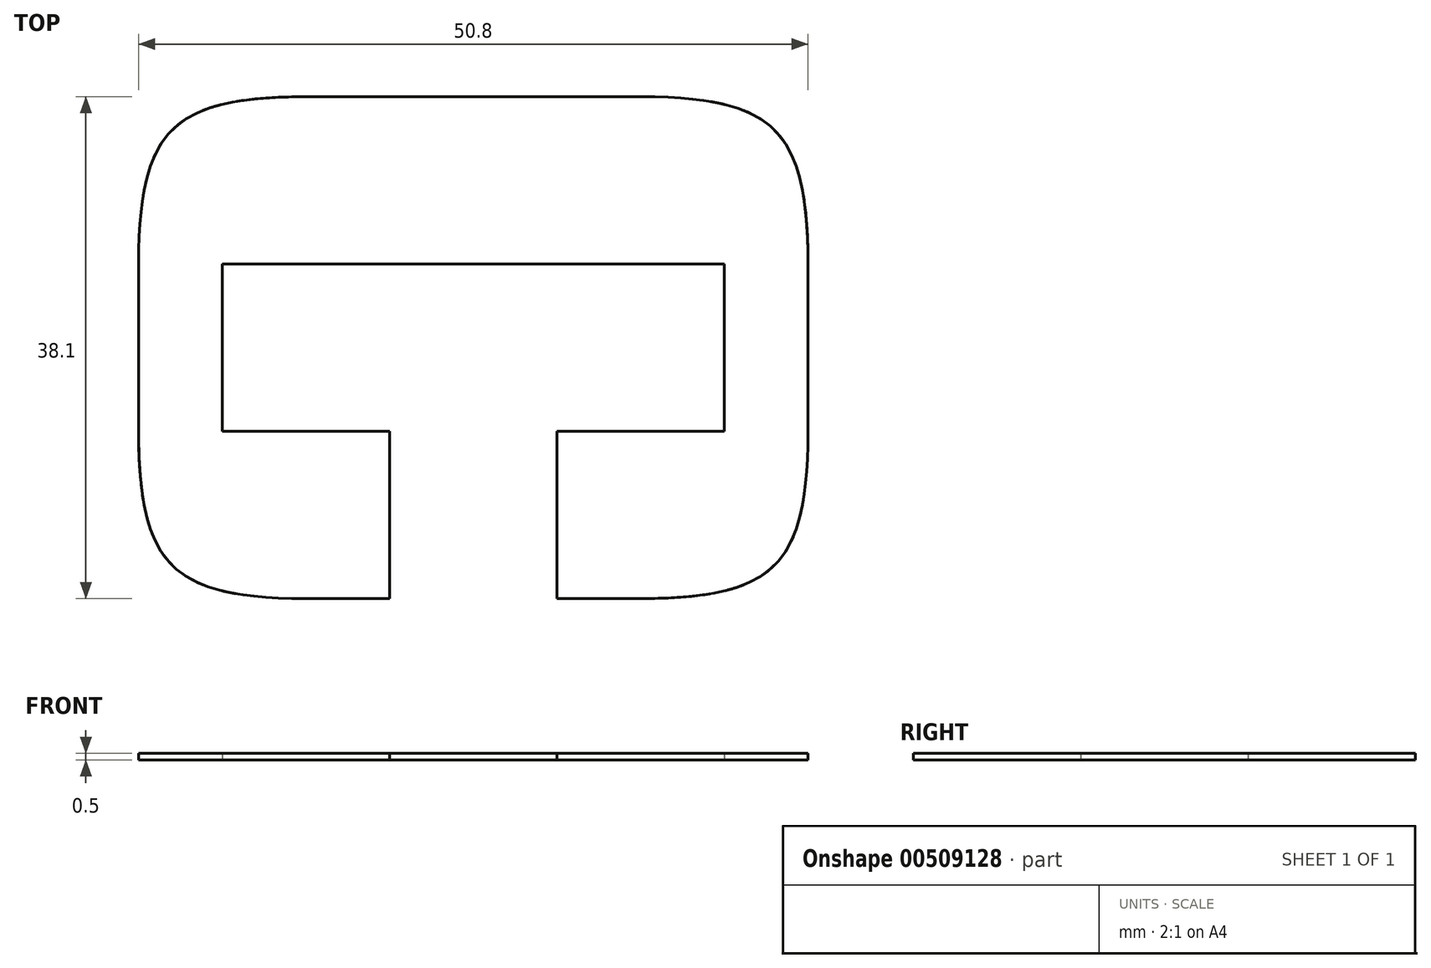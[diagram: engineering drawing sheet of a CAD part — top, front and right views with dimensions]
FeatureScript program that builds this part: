
annotation { "Feature Type Name" : "Feature", "Feature Type Description" : "" }
export const myFeature = defineFeature(function(context is Context, id is Id, definition is map)
    precondition{}
    {
        {
            assignVariable(context, id + "F0", {"name" : "mat_thk", "anyValue" : .5});
        }
        {
            var Q0;
            Q0=qCreatedBy(makeId("Top.planeOp"),FACE);
            var sketch = newSketch(context, id + "F1", { "sketchPlane" : qUnion([Q0])});
            skLineSegment(sketch, "E0.bottom", {"start": v(-25.4, 19.05) * mm, "end": v(25.4, 19.05) * mm});
            skLineSegment(sketch, "E0.top", {"start": v(-25.4, -19.05) * mm, "end": v(-6.35, -19.05) * mm});
            skLineSegment(sketch, "E0.left", {"start": v(-25.4, 19.05) * mm, "end": v(-25.4, -19.05) * mm});
            skLineSegment(sketch, "E0.right", {"start": v(25.4, 19.05) * mm, "end": v(25.4, -19.05) * mm});
            skLineSegment(sketch, "E1.bottom", {"start": v(-19.05, 6.35) * mm, "end": v(19.05, 6.35) * mm});
            skLineSegment(sketch, "E1.top", {"start": v(-19.05, -6.35) * mm, "end": v(-6.35, -6.35) * mm});
            skLineSegment(sketch, "E1.left", {"start": v(-19.05, 6.35) * mm, "end": v(-19.05, -6.35) * mm});
            skLineSegment(sketch, "E1.right", {"start": v(19.05, 6.35) * mm, "end": v(19.05, -6.35) * mm});
            skLineSegment(sketch, "E2", {"start": v(-6.35, -6.35) * mm, "end": v(-6.35, -19.05) * mm});
            skLineSegment(sketch, "E3", {"start": v(6.35, -6.35) * mm, "end": v(6.35, -19.05) * mm});
            skLineSegment(sketch, "E4.trimOffspring", {"start": v(6.35, -19.05) * mm, "end": v(25.4, -19.05) * mm});
            skLineSegment(sketch, "E5.trimOffspring", {"start": v(6.35, -6.35) * mm, "end": v(19.05, -6.35) * mm});
            skSolve(sketch);
        }
        {
            var Q0;
            Q0 = qSketchRegion(id + "F1", true);
            extrude(context, id + "F2", {"entities" : qUnion([Q0]), "endBound" : BoundingType.SYMMETRIC, "depth" : (getVariable(context, 'mat_thk')) * mm});
        }
        {
            var Q0;
            Q0=makeQuery(id+"F2.opExtrude","SWEPT_EDGE",EDGE,{"disambiguationData":[OSD([sQuery(id+"F1.wireOp",EDGE,"E0.right"),sQuery(id+"F1.wireOp",EDGE,"E4.trimOffspring")])]});
            var Q1;
            Q1=makeQuery(id+"F2.opExtrude","SWEPT_EDGE",EDGE,{"disambiguationData":[OSD([sQuery(id+"F1.wireOp",EDGE,"E0.bottom"),sQuery(id+"F1.wireOp",EDGE,"E0.right")])]});
            var Q2;
            Q2=makeQuery(id+"F2.opExtrude","SWEPT_EDGE",EDGE,{"disambiguationData":[OSD([sQuery(id+"F1.wireOp",EDGE,"E0.bottom"),sQuery(id+"F1.wireOp",EDGE,"E0.left")])]});
            var Q3;
            Q3=makeQuery(id+"F2.opExtrude","SWEPT_EDGE",EDGE,{"disambiguationData":[OSD([sQuery(id+"F1.wireOp",EDGE,"E0.top"),sQuery(id+"F1.wireOp",EDGE,"E0.left")])]});
            fillet(context, id + "F3", {"entities" : qUnion([Q0, Q1, Q2, Q3]), "radius" : 12.7 * mm, "rho" : .6, "crossSection" : FilletCrossSection.CONIC, "allowEdgeOverflow" : false});
        }
    });
